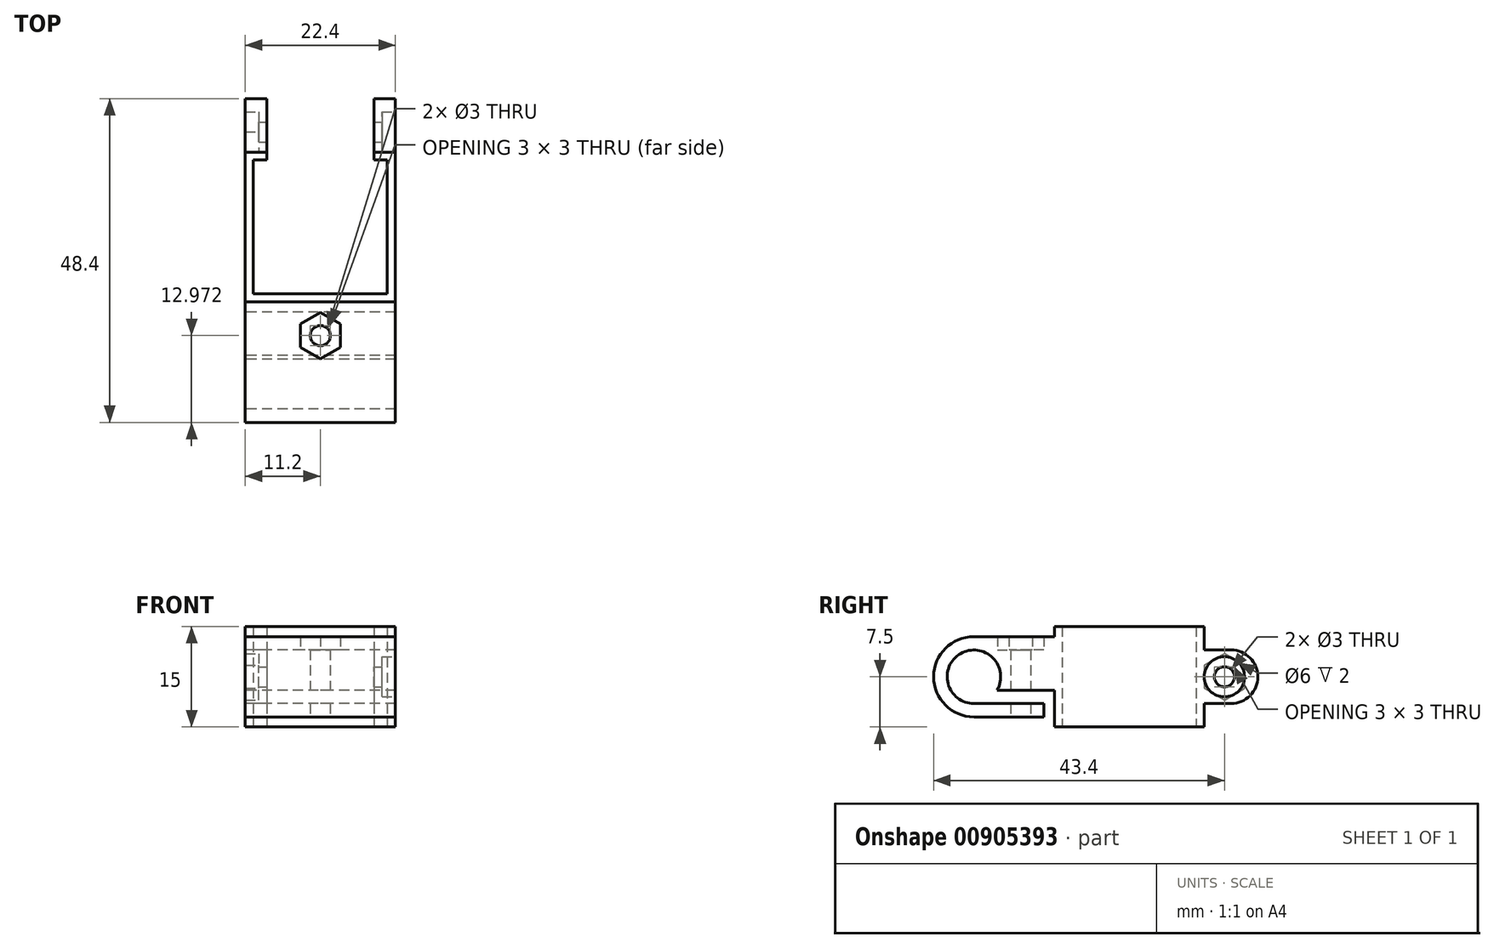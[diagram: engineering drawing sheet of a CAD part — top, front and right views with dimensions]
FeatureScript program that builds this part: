
annotation { "Feature Type Name" : "Feature", "Feature Type Description" : "" }
export const myFeature = defineFeature(function(context is Context, id is Id, definition is map)
    precondition{}
    {
        {
            var Q0;
            Q0=qCreatedBy(makeId("Top.planeOp"),FACE);
            var sketch = newSketch(context, id + "F0", { "sketchPlane" : qUnion([Q0])});
            skLineSegment(sketch, "E0.bottom", {"start": v(0, 0) * mm, "end": v(20, 0) * mm});
            skLineSegment(sketch, "E0.top", {"start": v(0, 20) * mm, "end": v(20, 20) * mm});
            skLineSegment(sketch, "E0.left", {"start": v(0, 0) * mm, "end": v(0, 20) * mm});
            skLineSegment(sketch, "E0.right", {"start": v(20, 0) * mm, "end": v(20, 20) * mm});
            skLineSegment(sketch, "E1.bottom", {"start": v(0, 0) * mm, "end": v(-1.2, 0) * mm, "construction": true});
            skLineSegment(sketch, "E1.top", {"start": v(0, -1.2) * mm, "end": v(-1.2, -1.2) * mm, "construction": true});
            skLineSegment(sketch, "E1.left", {"start": v(0, 0) * mm, "end": v(0, -1.2) * mm, "construction": true});
            skLineSegment(sketch, "E1.right", {"start": v(-1.2, 0) * mm, "end": v(-1.2, -1.2) * mm, "construction": true});
            skLineSegment(sketch, "E2.bottom", {"start": v(-1.2, -1.2) * mm, "end": v(21.2, -1.2) * mm});
            skLineSegment(sketch, "E2.top", {"start": v(-1.2, 21.2) * mm, "end": v(21.2, 21.2) * mm});
            skLineSegment(sketch, "E2.left", {"start": v(-1.2, -1.2) * mm, "end": v(-1.2, 21.2) * mm});
            skLineSegment(sketch, "E2.right", {"start": v(21.2, -1.2) * mm, "end": v(21.2, 21.2) * mm});
            skLineSegment(sketch, "E3", {"start": v(0, 20) * mm, "end": v(2, 20) * mm, "construction": true});
            skLineSegment(sketch, "E4", {"start": v(2, 20) * mm, "end": v(2, 21.2) * mm});
            skLineSegment(sketch, "E5", {"start": v(20, 20) * mm, "end": v(18, 20) * mm, "construction": true});
            skLineSegment(sketch, "E6", {"start": v(18, 20) * mm, "end": v(18, 21.2) * mm});
            skSolve(sketch);
        }
        {
            var Q0;
            Q0=makeQuery(id+"F0.imprint","IMPRINT",FACE,{"disambiguationData":[TD([[makeQuery(id+"F0.imprint","IMPRINT",EDGE,{"derivedFrom":sQuery(id+"F0.wireOp",EDGE,"E0.bottom")}),-1.0]])]});
            extrude(context, id + "F1", {"entities" : qUnion([Q0]), "depth" : 15 * mm, "offsetDistance" : 25 * mm});
        }
        {
            var Q0;
            Q0=makeQuery(id+"F1.opExtrude","SWEPT_FACE",FACE,{"disambiguationData":[OSD([sQuery(id+"F0.wireOp",EDGE,"E2.left")])]});
            var sketch = newSketch(context, id + "F2", { "sketchPlane" : qUnion([Q0])});
            skLineSegment(sketch, "E7", {"start": v(1.2, 7.5) * mm, "end": v(13.2, 7.5) * mm, "construction": true});
            skCircle(sketch, "E8", {"center": v(13.2, 7.5) * mm, "radius": 4 * mm});
            skCircle(sketch, "E9", {"center": v(13.2, 7.5) * mm, "radius": 6 * mm});
            skLineSegment(sketch, "E10", {"start": v(1.2, 7.5) * mm, "end": v(1.2, 13.5) * mm, "construction": true});
            skLineSegment(sketch, "E11", {"start": v(1.2, 13.5) * mm, "end": v(13.2, 13.5) * mm});
            skLineSegment(sketch, "E12", {"start": v(1.2, 7.5) * mm, "end": v(1.2, 1.5) * mm, "construction": true});
            skLineSegment(sketch, "E13", {"start": v(1.2, 1.5) * mm, "end": v(13.2, 1.5) * mm});
            skLineSegment(sketch, "E14", {"start": v(13.2, 7.5) * mm, "end": v(13.2, 3.5) * mm, "construction": true});
            skLineSegment(sketch, "E15", {"start": v(13.2, 3.5) * mm, "end": v(8.73, 3.5) * mm});
            skLineSegment(sketch, "E16", {"start": v(8.73, 3.5) * mm, "end": v(2.73, 3.5) * mm});
            skLineSegment(sketch, "E17", {"start": v(2.73, 3.5) * mm, "end": v(2.73, 1.5) * mm});
            skLineSegment(sketch, "E18", {"start": v(13.2, 7.5) * mm, "end": v(13.2, 5.5) * mm, "construction": true});
            skLineSegment(sketch, "E19", {"start": v(13.2, 5.5) * mm, "end": v(1.2, 5.5) * mm});
            skSolve(sketch);
        }
        {
            var Q0;
            {var subQ0=sQuery(id+"F2.wireOp",EDGE,"E11");Q0=makeQuery(id+"F2.imprint","IMPRINT",FACE,{"disambiguationData":[TD([[makeQuery(id+"F2.imprint","IMPRINT",EDGE,{"derivedFrom":subQ0}),-1.0]])]});}
            var Q1;
            {var subQ3=sQuery(id+"F2.wireOp",EDGE,"E15");Q1=makeQuery(id+"F2.imprint","IMPRINT",FACE,{"disambiguationData":[TD([[makeQuery(id+"F2.imprint","IMPRINT",EDGE,{"derivedFrom":subQ3}),1.0]])]});}
            var Q2;
            {var subQ3=sQuery(id+"F2.wireOp",EDGE,"E16");Q2=makeQuery(id+"F2.imprint","IMPRINT",FACE,{"disambiguationData":[TD([[makeQuery(id+"F2.imprint","IMPRINT",EDGE,{"derivedFrom":subQ3}),1.0]])]});}
            extrude(context, id + "F3", {"entities" : qUnion([Q0, Q1, Q2]), "operationType" : NewBodyOperationType.ADD, "oppositeDirection" : true, "depth" : 22.4 * mm, "offsetDistance" : 25 * mm});
        }
        {
            var Q0;
            Q0=makeQuery(id+"F3.opExtrude","SWEPT_FACE",FACE,{"disambiguationData":[OSD([sQuery(id+"F2.wireOp",EDGE,"E13")])]});
            var sketch = newSketch(context, id + "F4", { "sketchPlane" : qUnion([Q0])});
            skLineSegment(sketch, "E20", {"start": v(10, 2.73) * mm, "end": v(10, 6.23) * mm});
            skCircle(sketch, "E21", {"center": v(10, 6.23) * mm, "radius": 1.5 * mm});
            skLineSegment(sketch, "E22", {"start": v(10, 6.23) * mm, "end": v(7, 6.23) * mm});
            skCircle(sketch, "E23.cCircle", {"center": v(10, 6.23) * mm, "radius": 3 * mm, "construction": true});
            skLineSegment(sketch, "E23.0", {"start": v(7, 4.5) * mm, "end": v(7, 7.96) * mm});
            skLineSegment(sketch, "E23.1", {"start": v(7, 7.96) * mm, "end": v(10, 9.7) * mm});
            skLineSegment(sketch, "E23.2", {"start": v(10, 9.7) * mm, "end": v(13, 7.96) * mm});
            skLineSegment(sketch, "E23.3", {"start": v(13, 7.96) * mm, "end": v(13, 4.5) * mm});
            skLineSegment(sketch, "E23.4", {"start": v(13, 4.5) * mm, "end": v(10, 2.76) * mm});
            skLineSegment(sketch, "E23.5", {"start": v(10, 2.76) * mm, "end": v(7, 4.5) * mm});
            skPoint(sketch, "E23.0.midPoint", {"position": v(7, 6.23) * mm});
            skSolve(sketch);
        }
        {
            var Q0;
            Q0=makeQuery(id+"F4.imprint","IMPRINT",FACE,{"disambiguationData":[TD([[makeQuery(id+"F4.imprint","IMPRINT",EDGE,{"derivedFrom":sQuery(id+"F4.wireOp",EDGE,"E21")}),1.0]])]});
            extrude(context, id + "F5", {"entities" : qUnion([Q0]), "operationType" : NewBodyOperationType.REMOVE, "oppositeDirection" : true, "depth" : 25 * mm, "offsetDistance" : 25 * mm});
        }
        {
            var Q0;
            {var subQ3=sQuery(id+"F4.wireOp",EDGE,"E23.1");Q0=makeQuery(id+"F4.imprint","IMPRINT",FACE,{"disambiguationData":[TD([[makeQuery(id+"F4.imprint","IMPRINT",EDGE,{"derivedFrom":subQ3}),-1.0]])]});}
            var Q1;
            {var subQ3=sQuery(id+"F4.wireOp",EDGE,"E23.5");Q1=makeQuery(id+"F4.imprint","IMPRINT",FACE,{"disambiguationData":[TD([[makeQuery(id+"F4.imprint","IMPRINT",EDGE,{"derivedFrom":subQ3}),-1.0]])]});}
            extrude(context, id + "F6", {"entities" : qUnion([Q0, Q1]), "operationType" : NewBodyOperationType.REMOVE, "oppositeDirection" : true, "depth" : 25 * mm, "offsetDistance" : 25 * mm, "hasSecondDirection" : true, "secondDirectionOppositeDirection" : true, "secondDirectionDepth" : 10 * mm});
        }
        {
            var Q0;
            {var subQ0=sQuery(id+"F0.wireOp",EDGE,"E2.top");Q0=makeQuery(id+"F1.opExtrude","SWEPT_FACE",FACE,{"disambiguationData":[OSD([subQ0]),TDD([makeQuery(id+"F0.imprint","IMPRINT",EDGE,{"disambiguationData":[TD([[makeQuery(id+"F0.imprint","INTERSECT",VERTEX,{"derivedFrom":[subQ0,sQuery(id+"F0.wireOp",EDGE,"E2.right")]}),1.0]])],"derivedFrom":subQ0})])]});}
            var sketch = newSketch(context, id + "F7", { "sketchPlane" : qUnion([Q0])});
            skLineSegment(sketch, "E24", {"start": v(-21.2, 15) * mm, "end": v(-21.2, 11.5) * mm, "construction": true});
            skLineSegment(sketch, "E25.bottom", {"start": v(-21.2, 11.5) * mm, "end": v(-18, 11.5) * mm});
            skLineSegment(sketch, "E25.top", {"start": v(-21.2, 3.5) * mm, "end": v(-18, 3.5) * mm});
            skLineSegment(sketch, "E25.left", {"start": v(-21.2, 11.5) * mm, "end": v(-21.2, 3.5) * mm});
            skLineSegment(sketch, "E25.right", {"start": v(-18, 11.5) * mm, "end": v(-18, 3.5) * mm});
            skLineSegment(sketch, "E26", {"start": v(-18, 3.5) * mm, "end": v(-2, 3.5) * mm, "construction": true});
            skLineSegment(sketch, "E27.bottom", {"start": v(-2, 3.5) * mm, "end": v(1.2, 3.5) * mm});
            skLineSegment(sketch, "E27.top", {"start": v(-2, 11.5) * mm, "end": v(1.2, 11.5) * mm});
            skLineSegment(sketch, "E27.left", {"start": v(-2, 3.5) * mm, "end": v(-2, 11.5) * mm});
            skLineSegment(sketch, "E27.right", {"start": v(1.2, 3.5) * mm, "end": v(1.2, 11.5) * mm});
            skSolve(sketch);
        }
        {
            var Q0;
            Q0=makeQuery(id+"F7.imprint","IMPRINT",FACE,{"disambiguationData":[TD([[makeQuery(id+"F7.imprint","IMPRINT",EDGE,{"derivedFrom":sQuery(id+"F7.wireOp",EDGE,"E25.bottom")}),-1.0]])]});
            var Q1;
            Q1=makeQuery(id+"F7.imprint","IMPRINT",FACE,{"disambiguationData":[TD([[makeQuery(id+"F7.imprint","IMPRINT",EDGE,{"derivedFrom":sQuery(id+"F7.wireOp",EDGE,"E27.bottom")}),1.0]])]});
            extrude(context, id + "F8", {"entities" : qUnion([Q0, Q1]), "operationType" : NewBodyOperationType.ADD, "depth" : 8 * mm, "offsetDistance" : 25 * mm});
        }
        {
            var Q0;
            Q0=makeQuery(id+"F8.opExtrude","CAP_EDGE",EDGE,{"disambiguationData":[OSD([sQuery(id+"F7.wireOp",EDGE,"E25.bottom")])],"isStart":false});
            var Q1;
            Q1=makeQuery(id+"F8.opExtrude","CAP_EDGE",EDGE,{"disambiguationData":[OSD([sQuery(id+"F7.wireOp",EDGE,"E25.top")])],"isStart":false});
            var Q2;
            Q2=makeQuery(id+"F8.opExtrude","CAP_EDGE",EDGE,{"disambiguationData":[OSD([sQuery(id+"F7.wireOp",EDGE,"E27.top")])],"isStart":false});
            var Q3;
            Q3=makeQuery(id+"F8.opExtrude","CAP_EDGE",EDGE,{"disambiguationData":[OSD([sQuery(id+"F7.wireOp",EDGE,"E27.bottom")])],"isStart":false});
            fillet(context, id + "F9", {"entities" : qUnion([Q0, Q1, Q2, Q3]), "radius" : 4 * mm, "tangentPropagation" : true, "allowEdgeOverflow" : false});
        }
        {
            var Q0;
            Q0=makeQuery(id+"F8.boolean.opBoolean","MERGE",FACE,{"derivedFrom":[makeQuery(id+"F3.boolean.opBoolean","MERGE",FACE,{"derivedFrom":[makeQuery(id+"F1.opExtrude","SWEPT_FACE",FACE,{"disambiguationData":[OSD([sQuery(id+"F0.wireOp",EDGE,"E2.right")])]}),makeQuery(id+"F3.opExtrude","CAP_FACE",FACE,{"disambiguationData":[OSD([sQuery(id+"F0.wireOp",EDGE,"E2.bottom"),sQuery(id+"F0.wireOp",EDGE,"E2.left"),sQuery(id+"F2.wireOp",EDGE,"E8"),sQuery(id+"F2.wireOp",EDGE,"E9"),sQuery(id+"F2.wireOp",EDGE,"E11"),sQuery(id+"F2.wireOp",EDGE,"E13"),sQuery(id+"F2.wireOp",EDGE,"E15"),sQuery(id+"F2.wireOp",EDGE,"E16"),sQuery(id+"F2.wireOp",EDGE,"E17"),sQuery(id+"F2.wireOp",EDGE,"E19")])],"isStart":false})]}),makeQuery(id+"F8.opExtrude","SWEPT_FACE",FACE,{"disambiguationData":[OSD([sQuery(id+"F7.wireOp",EDGE,"E25.left")])]})]});
            var sketch = newSketch(context, id + "F10", { "sketchPlane" : qUnion([Q0])});
            skLineSegment(sketch, "E28.bottom", {"start": v(21.2, 11.5) * mm, "end": v(24.2, 11.5) * mm, "construction": true});
            skLineSegment(sketch, "E28.top", {"start": v(21.2, 7.5) * mm, "end": v(24.2, 7.5) * mm, "construction": true});
            skLineSegment(sketch, "E28.left", {"start": v(21.2, 11.5) * mm, "end": v(21.2, 7.5) * mm, "construction": true});
            skLineSegment(sketch, "E28.right", {"start": v(24.2, 11.5) * mm, "end": v(24.2, 7.5) * mm, "construction": true});
            skCircle(sketch, "E29", {"center": v(24.2, 7.5) * mm, "radius": 1.5 * mm});
            skCircle(sketch, "E30", {"center": v(24.2, 7.5) * mm, "radius": 3 * mm});
            skCircle(sketch, "E31.cCircle", {"center": v(24.2, 7.5) * mm, "radius": 3 * mm, "construction": true});
            skLineSegment(sketch, "E31.0", {"start": v(21.2, 5.77) * mm, "end": v(21.2, 9.23) * mm});
            skLineSegment(sketch, "E31.1", {"start": v(21.2, 9.23) * mm, "end": v(24.2, 10.96) * mm});
            skLineSegment(sketch, "E31.2", {"start": v(24.2, 10.96) * mm, "end": v(27.2, 9.23) * mm});
            skLineSegment(sketch, "E31.3", {"start": v(27.2, 9.23) * mm, "end": v(27.2, 5.77) * mm});
            skLineSegment(sketch, "E31.4", {"start": v(27.2, 5.77) * mm, "end": v(24.2, 4.04) * mm});
            skLineSegment(sketch, "E31.5", {"start": v(24.2, 4.04) * mm, "end": v(21.2, 5.77) * mm});
            skPoint(sketch, "E31.0.midPoint", {"position": v(21.2, 7.5) * mm});
            skSolve(sketch);
        }
        {
            var Q0;
            Q0=makeQuery(id+"F10.imprint","IMPRINT",FACE,{"disambiguationData":[TD([[makeQuery(id+"F10.imprint","IMPRINT",EDGE,{"derivedFrom":sQuery(id+"F10.wireOp",EDGE,"E29")}),1.0]])]});
            extrude(context, id + "F11", {"entities" : qUnion([Q0]), "operationType" : NewBodyOperationType.REMOVE, "oppositeDirection" : true, "depth" : 25 * mm, "offsetDistance" : 25 * mm});
        }
        {
            var Q0;
            Q0=makeQuery(id+"F10.imprint","IMPRINT",FACE,{"disambiguationData":[TD([[makeQuery(id+"F10.imprint","IMPRINT",EDGE,{"derivedFrom":sQuery(id+"F10.wireOp",EDGE,"E29")}),-1.0]])]});
            extrude(context, id + "F12", {"entities" : qUnion([Q0]), "operationType" : NewBodyOperationType.REMOVE, "oppositeDirection" : true, "depth" : 2 * mm, "offsetDistance" : 25 * mm});
        }
        {
            var Q0;
            {var subQ0=sQuery(id+"F10.wireOp",EDGE,"E31.1");var subQ1=sQuery(id+"F10.wireOp",EDGE,"E30");var subQ2=makeQuery(id+"F10.imprint","INTERSECT",VERTEX,{"derivedFrom":[subQ1,subQ0]});Q0=makeQuery(id+"F10.imprint","IMPRINT",FACE,{"disambiguationData":[TD([[makeQuery(id+"F10.imprint","IMPRINT",EDGE,{"disambiguationData":[TD([[subQ2,-1.0]])],"derivedFrom":subQ1}),-1.0]])]});}
            var Q1;
            {var subQ0=sQuery(id+"F10.wireOp",EDGE,"E31.2");var subQ1=sQuery(id+"F10.wireOp",EDGE,"E30");var subQ2=makeQuery(id+"F10.imprint","INTERSECT",VERTEX,{"derivedFrom":[subQ1,subQ0]});Q1=makeQuery(id+"F10.imprint","IMPRINT",FACE,{"disambiguationData":[TD([[makeQuery(id+"F10.imprint","IMPRINT",EDGE,{"disambiguationData":[TD([[subQ2,-1.0]])],"derivedFrom":subQ1}),-1.0]])]});}
            var Q2;
            {var subQ0=sQuery(id+"F10.wireOp",EDGE,"E31.2");var subQ1=sQuery(id+"F10.wireOp",EDGE,"E30");var subQ2=makeQuery(id+"F10.imprint","INTERSECT",VERTEX,{"derivedFrom":[subQ1,subQ0]});Q2=makeQuery(id+"F10.imprint","IMPRINT",FACE,{"disambiguationData":[TD([[makeQuery(id+"F10.imprint","IMPRINT",EDGE,{"disambiguationData":[TD([[subQ2,1.0]])],"derivedFrom":subQ1}),-1.0]])]});}
            var Q3;
            Q3=makeQuery(id+"F10.imprint","IMPRINT",FACE,{"disambiguationData":[TD([[makeQuery(id+"F10.imprint","IMPRINT",EDGE,{"derivedFrom":sQuery(id+"F10.wireOp",EDGE,"E29")}),-1.0]])]});
            var Q4;
            {var subQ0=sQuery(id+"F10.wireOp",EDGE,"E31.5");var subQ1=sQuery(id+"F10.wireOp",EDGE,"E30");var subQ2=makeQuery(id+"F10.imprint","INTERSECT",VERTEX,{"derivedFrom":[subQ1,subQ0]});Q4=makeQuery(id+"F10.imprint","IMPRINT",FACE,{"disambiguationData":[TD([[makeQuery(id+"F10.imprint","IMPRINT",EDGE,{"disambiguationData":[TD([[subQ2,-1.0]])],"derivedFrom":subQ1}),-1.0]])]});}
            var Q5;
            {var subQ0=sQuery(id+"F10.wireOp",EDGE,"E31.0");var subQ1=sQuery(id+"F10.wireOp",EDGE,"E30");var subQ2=makeQuery(id+"F10.imprint","INTERSECT",VERTEX,{"derivedFrom":[subQ1,subQ0]});Q5=makeQuery(id+"F10.imprint","IMPRINT",FACE,{"disambiguationData":[TD([[makeQuery(id+"F10.imprint","IMPRINT",EDGE,{"disambiguationData":[TD([[subQ2,-1.0]])],"derivedFrom":subQ1}),-1.0]])]});}
            var Q6;
            {var subQ0=sQuery(id+"F10.wireOp",EDGE,"E31.3");var subQ1=sQuery(id+"F10.wireOp",EDGE,"E30");var subQ2=makeQuery(id+"F10.imprint","INTERSECT",VERTEX,{"derivedFrom":[subQ1,subQ0]});Q6=makeQuery(id+"F10.imprint","IMPRINT",FACE,{"disambiguationData":[TD([[makeQuery(id+"F10.imprint","IMPRINT",EDGE,{"disambiguationData":[TD([[subQ2,1.0]])],"derivedFrom":subQ1}),-1.0]])]});}
            extrude(context, id + "F13", {"entities" : qUnion([Q0, Q1, Q2, Q3, Q4, Q5, Q6]), "operationType" : NewBodyOperationType.REMOVE, "oppositeDirection" : true, "depth" : 25 * mm, "offsetDistance" : 25 * mm, "hasSecondDirection" : true, "secondDirectionOppositeDirection" : true, "secondDirectionDepth" : 20.4 * mm});
        }
    });
